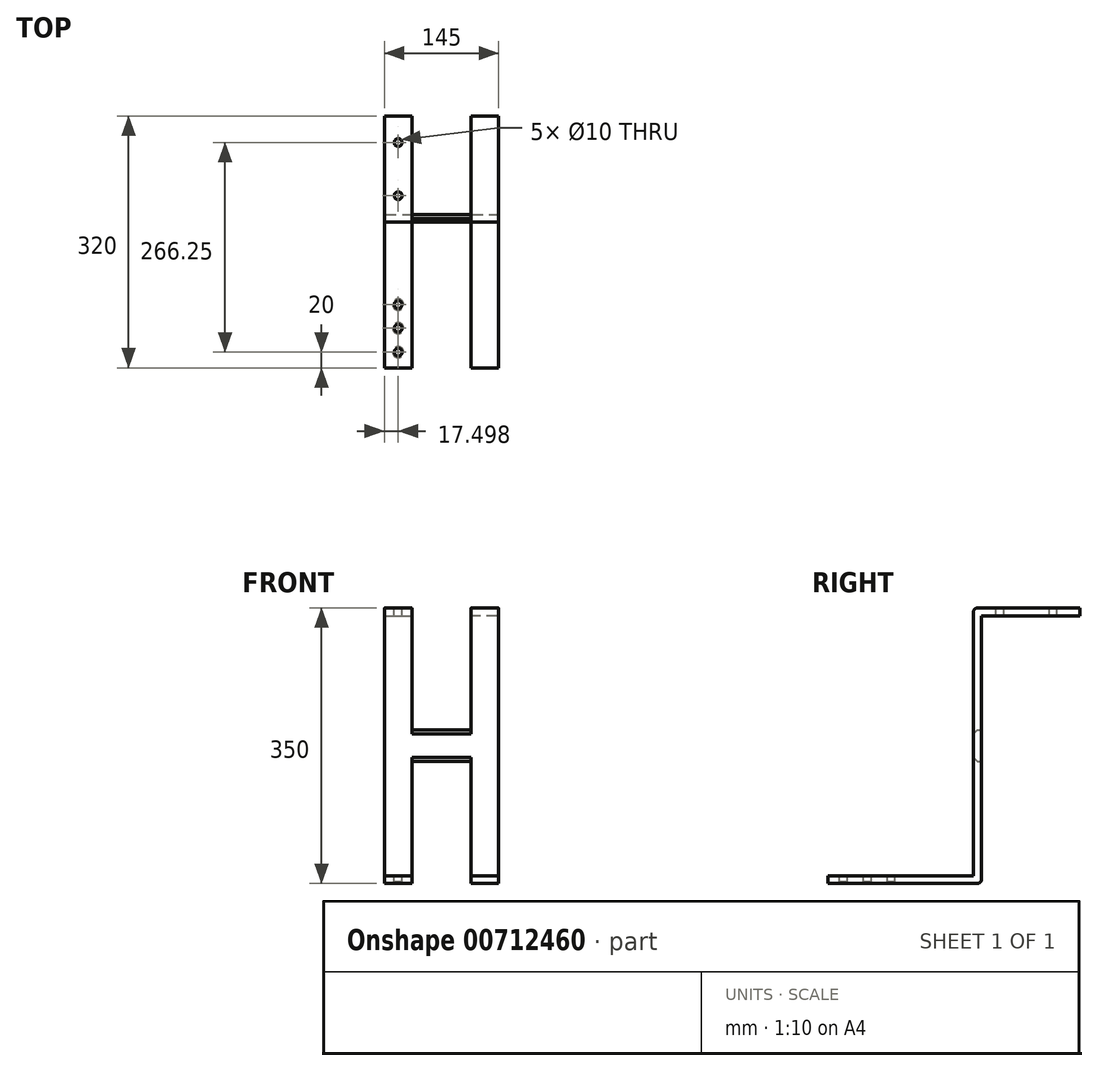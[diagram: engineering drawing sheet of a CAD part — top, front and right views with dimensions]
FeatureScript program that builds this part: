
annotation { "Feature Type Name" : "Feature", "Feature Type Description" : "" }
export const myFeature = defineFeature(function(context is Context, id is Id, definition is map)
    precondition{}
    {
        {
            var Q0;
            Q0=qCreatedBy(makeId("Front.planeOp"),FACE);
            var sketch = newSketch(context, id + "F0", { "sketchPlane" : qUnion([Q0])});
            skLineSegment(sketch, "E0.bottom", {"start": v(-69.95, 272.66) * mm, "end": v(-34.95, 272.66) * mm});
            skLineSegment(sketch, "E0.top", {"start": v(-69.95, -77.34) * mm, "end": v(-34.95, -77.34) * mm});
            skLineSegment(sketch, "E0.left", {"start": v(-69.95, 272.66) * mm, "end": v(-69.95, -77.34) * mm});
            skLineSegment(sketch, "E0.right", {"start": v(-34.95, 272.66) * mm, "end": v(-34.95, -77.34) * mm});
            skLineSegment(sketch, "E1.bottom", {"start": v(40.05, 272.66) * mm, "end": v(75.05, 272.66) * mm});
            skLineSegment(sketch, "E1.top", {"start": v(40.05, -77.34) * mm, "end": v(75.05, -77.34) * mm});
            skLineSegment(sketch, "E1.left", {"start": v(40.05, 272.66) * mm, "end": v(40.05, -77.34) * mm});
            skLineSegment(sketch, "E1.right", {"start": v(75.05, 272.66) * mm, "end": v(75.05, -77.34) * mm});
            skLineSegment(sketch, "E2", {"start": v(-34.95, 97.66) * mm, "end": v(-34.95, 117.66) * mm});
            skLineSegment(sketch, "E3.bottom", {"start": v(-34.95, 117.66) * mm, "end": v(40.05, 117.66) * mm});
            skLineSegment(sketch, "E3.top", {"start": v(-34.95, 77.66) * mm, "end": v(40.05, 77.66) * mm});
            skSolve(sketch);
        }
        {
            var Q0;
            Q0 = qSketchRegion(id + "F0", true);
            extrude(context, id + "F1", {"entities" : qUnion([Q0]), "depth" : 10 * mm, "offsetDistance" : 25 * mm});
        }
        {
            var Q0;
            Q0=makeQuery(id+"F1.opExtrude","CAP_FACE",FACE,{"disambiguationData":[OSD([sQuery(id+"F0.wireOp",EDGE,"E0.bottom"),sQuery(id+"F0.wireOp",EDGE,"E0.top"),sQuery(id+"F0.wireOp",EDGE,"E0.left"),sQuery(id+"F0.wireOp",EDGE,"E0.right"),sQuery(id+"F0.wireOp",EDGE,"E1.bottom"),sQuery(id+"F0.wireOp",EDGE,"E1.top"),sQuery(id+"F0.wireOp",EDGE,"E1.left"),sQuery(id+"F0.wireOp",EDGE,"E1.right"),sQuery(id+"F0.wireOp",EDGE,"E3.bottom"),sQuery(id+"F0.wireOp",EDGE,"E3.top")])],"isStart":false});
            var sketch = newSketch(context, id + "F2", { "sketchPlane" : qUnion([Q0])});
            skLineSegment(sketch, "E4", {"start": v(-69.95, -77.34) * mm, "end": v(-34.95, -77.34) * mm});
            skLineSegment(sketch, "E5", {"start": v(-34.95, -77.34) * mm, "end": v(-34.95, -67.34) * mm});
            skLineSegment(sketch, "E6.bottom", {"start": v(-34.95, -67.34) * mm, "end": v(-69.95, -67.34) * mm});
            skLineSegment(sketch, "E6.top", {"start": v(-34.95, -77.34) * mm, "end": v(-69.95, -77.34) * mm});
            skLineSegment(sketch, "E6.right", {"start": v(-69.95, -67.34) * mm, "end": v(-69.95, -77.34) * mm});
            skLineSegment(sketch, "E7", {"start": v(2.55, 77.66) * mm, "end": v(2.55, -129.94) * mm});
            skLineSegment(sketch, "E8.MirrorCS", {"start": v(40.05, -77.34) * mm, "end": v(40.05, -67.34) * mm});
            skLineSegment(sketch, "E9.MirrorCS", {"start": v(40.05, -77.34) * mm, "end": v(75.05, -77.34) * mm});
            skLineSegment(sketch, "E10.MirrorCS", {"start": v(40.05, -67.34) * mm, "end": v(75.05, -67.34) * mm});
            skLineSegment(sketch, "E11.MirrorCS", {"start": v(75.05, -67.34) * mm, "end": v(75.05, -77.34) * mm});
            skSolve(sketch);
        }
        {
            var Q0;
            Q0=makeQuery(id+"F2.imprint","IMPRINT",FACE,{"disambiguationData":[TD([[makeQuery(id+"F2.imprint","IMPRINT",EDGE,{"derivedFrom":sQuery(id+"F2.wireOp",EDGE,"E5")}),-1.0]])]});
            var Q1;
            Q1=makeQuery(id+"F2.imprint","IMPRINT",FACE,{"disambiguationData":[TD([[makeQuery(id+"F2.imprint","IMPRINT",EDGE,{"derivedFrom":sQuery(id+"F2.wireOp",EDGE,"E8.MirrorCS")}),1.0]])]});
            extrude(context, id + "F3", {"entities" : qUnion([Q0, Q1]), "operationType" : NewBodyOperationType.ADD, "depth" : 185 * mm, "offsetDistance" : 25 * mm});
        }
        {
            var Q0;
            Q0=makeQuery(id+"F3.opExtrude","SWEPT_FACE",FACE,{"disambiguationData":[OSD([sQuery(id+"F2.wireOp",EDGE,"E6.bottom")])]});
            var sketch = newSketch(context, id + "F4", { "sketchPlane" : qUnion([Q0])});
            skLineSegment(sketch, "E12", {"start": v(-34.95, -10) * mm, "end": v(40.05, -10) * mm});
            skLineSegment(sketch, "E13", {"start": v(2.55, -10) * mm, "end": v(2.55, -269.88) * mm});
            skLineSegment(sketch, "E14", {"start": v(-69.95, -195) * mm, "end": v(-69.95, -175) * mm});
            skLineSegment(sketch, "E15", {"start": v(-69.95, -175) * mm, "end": v(-69.95, -159.54) * mm});
            skLineSegment(sketch, "E16", {"start": v(-69.95, -159.54) * mm, "end": v(-69.95, -144.54) * mm});
            skLineSegment(sketch, "E17", {"start": v(-69.95, -144.54) * mm, "end": v(-69.95, -129.54) * mm});
            skLineSegment(sketch, "E18", {"start": v(-69.95, -129.54) * mm, "end": v(-69.95, -114.54) * mm});
            skLineSegment(sketch, "E19", {"start": v(-69.95, -114.54) * mm, "end": v(-69.95, -99.54) * mm});
            skCircle(sketch, "E20", {"center": v(-52.45, -114.54) * mm, "radius": 5 * mm});
            skCircle(sketch, "E21", {"center": v(-52.45, -144.54) * mm, "radius": 5 * mm});
            skCircle(sketch, "E22", {"center": v(-52.45, -175) * mm, "radius": 5 * mm});
            skCircle(sketch, "E23.MirrorC", {"center": v(57.55, -144.54) * mm, "radius": 5 * mm});
            skCircle(sketch, "E24.MirrorC", {"center": v(57.55, -175) * mm, "radius": 5 * mm});
            skCircle(sketch, "E25.MirrorC", {"center": v(57.55, -114.54) * mm, "radius": 5 * mm});
            skSolve(sketch);
        }
        {
            var Q0;
            Q0=makeQuery(id+"F4.imprint","IMPRINT",FACE,{"disambiguationData":[TD([[makeQuery(id+"F4.imprint","IMPRINT",EDGE,{"derivedFrom":sQuery(id+"F4.wireOp",EDGE,"E25.MirrorC")}),-1.0]])]});
            var Q1;
            Q1=makeQuery(id+"F4.imprint","IMPRINT",FACE,{"disambiguationData":[TD([[makeQuery(id+"F4.imprint","IMPRINT",EDGE,{"derivedFrom":sQuery(id+"F4.wireOp",EDGE,"E23.MirrorC")}),-1.0]])]});
            var Q2;
            Q2=makeQuery(id+"F4.imprint","IMPRINT",FACE,{"disambiguationData":[TD([[makeQuery(id+"F4.imprint","IMPRINT",EDGE,{"derivedFrom":sQuery(id+"F4.wireOp",EDGE,"E24.MirrorC")}),-1.0]])]});
            var Q3;
            Q3=makeQuery(id+"F4.imprint","IMPRINT",FACE,{"disambiguationData":[TD([[makeQuery(id+"F4.imprint","IMPRINT",EDGE,{"derivedFrom":sQuery(id+"F4.wireOp",EDGE,"E20")}),1.0]])]});
            var Q4;
            Q4=makeQuery(id+"F4.imprint","IMPRINT",FACE,{"disambiguationData":[TD([[makeQuery(id+"F4.imprint","IMPRINT",EDGE,{"derivedFrom":sQuery(id+"F4.wireOp",EDGE,"E21")}),1.0]])]});
            var Q5;
            Q5=makeQuery(id+"F4.imprint","IMPRINT",FACE,{"disambiguationData":[TD([[makeQuery(id+"F4.imprint","IMPRINT",EDGE,{"derivedFrom":sQuery(id+"F4.wireOp",EDGE,"E22")}),1.0]])]});
            extrude(context, id + "F5", {"entities" : qUnion([Q0, Q1, Q2, Q3, Q4, Q5]), "operationType" : NewBodyOperationType.REMOVE, "oppositeDirection" : true, "depth" : 25 * mm, "offsetDistance" : 25 * mm});
        }
        {
            var Q0;
            Q0=makeQuery(id+"F1.opExtrude","CAP_FACE",FACE,{"disambiguationData":[OSD([sQuery(id+"F0.wireOp",EDGE,"E0.bottom"),sQuery(id+"F0.wireOp",EDGE,"E0.top"),sQuery(id+"F0.wireOp",EDGE,"E0.left"),sQuery(id+"F0.wireOp",EDGE,"E0.right"),sQuery(id+"F0.wireOp",EDGE,"E1.bottom"),sQuery(id+"F0.wireOp",EDGE,"E1.top"),sQuery(id+"F0.wireOp",EDGE,"E1.left"),sQuery(id+"F0.wireOp",EDGE,"E1.right"),sQuery(id+"F0.wireOp",EDGE,"E3.bottom"),sQuery(id+"F0.wireOp",EDGE,"E3.top")])],"isStart":true});
            var sketch = newSketch(context, id + "F6", { "sketchPlane" : qUnion([Q0])});
            skLineSegment(sketch, "E26.bottom", {"start": v(-75.05, 272.66) * mm, "end": v(-40.05, 272.66) * mm});
            skLineSegment(sketch, "E26.top", {"start": v(-75.05, 262.66) * mm, "end": v(-40.05, 262.66) * mm});
            skLineSegment(sketch, "E26.left", {"start": v(-75.05, 272.66) * mm, "end": v(-75.05, 262.66) * mm});
            skLineSegment(sketch, "E26.right", {"start": v(-40.05, 272.66) * mm, "end": v(-40.05, 262.66) * mm});
            skLineSegment(sketch, "E27", {"start": v(-2.55, 195.16) * mm, "end": v(-2.55, 321.3) * mm});
            skLineSegment(sketch, "E28.MirrorCS", {"start": v(69.95, 262.66) * mm, "end": v(34.95, 262.66) * mm});
            skLineSegment(sketch, "E29.MirrorCS", {"start": v(34.95, 272.66) * mm, "end": v(34.95, 262.66) * mm});
            skLineSegment(sketch, "E30.MirrorCS", {"start": v(69.95, 272.66) * mm, "end": v(34.95, 272.66) * mm});
            skSolve(sketch);
        }
        {
            var Q0;
            Q0=makeQuery(id+"F6.imprint","IMPRINT",FACE,{"disambiguationData":[TD([[makeQuery(id+"F6.imprint","IMPRINT",EDGE,{"derivedFrom":sQuery(id+"F6.wireOp",EDGE,"E26.bottom")}),1.0]])]});
            var Q1;
            {var subQ0=sQuery(id+"F6.wireOp",EDGE,"E28.MirrorCS");Q1=makeQuery(id+"F6.imprint","IMPRINT",FACE,{"disambiguationData":[TD([[makeQuery(id+"F6.imprint","IMPRINT",EDGE,{"derivedFrom":subQ0}),-1.0]])]});}
            extrude(context, id + "F7", {"entities" : qUnion([Q0, Q1]), "operationType" : NewBodyOperationType.ADD, "depth" : 125 * mm, "offsetDistance" : 25 * mm});
        }
        {
            var Q0;
            Q0=makeQuery(id+"F7.boolean.opBoolean","MERGE",FACE,{"derivedFrom":[makeQuery(id+"F1.opExtrude","SWEPT_FACE",FACE,{"disambiguationData":[OSD([sQuery(id+"F0.wireOp",EDGE,"E0.bottom")])]}),makeQuery(id+"F7.opExtrude","SWEPT_FACE",FACE,{"disambiguationData":[OSD([sQuery(id+"F6.wireOp",EDGE,"E30.MirrorCS")])]})]});
            var sketch = newSketch(context, id + "F8", { "sketchPlane" : qUnion([Q0])});
            skLineSegment(sketch, "E31", {"start": v(-34.95, 57.5) * mm, "end": v(40.05, 57.5) * mm});
            skLineSegment(sketch, "E32", {"start": v(2.55, 57.5) * mm, "end": v(2.55, 287.25) * mm});
            skLineSegment(sketch, "E33", {"start": v(-34.95, 57.5) * mm, "end": v(-34.95, -10) * mm});
            skCircle(sketch, "E34", {"center": v(-52.45, 91.25) * mm, "radius": 5 * mm});
            skCircle(sketch, "E35", {"center": v(-52.45, 23.75) * mm, "radius": 5 * mm});
            skLineSegment(sketch, "E36", {"start": v(2.55, 57.5) * mm, "end": v(2.55, -29.78) * mm});
            skCircle(sketch, "E37.MirrorC", {"center": v(57.55, 23.75) * mm, "radius": 5 * mm});
            skCircle(sketch, "E38.MirrorC", {"center": v(57.55, 91.25) * mm, "radius": 5 * mm});
            skSolve(sketch);
        }
        {
            var Q0;
            Q0=makeQuery(id+"F8.imprint","IMPRINT",FACE,{"disambiguationData":[TD([[makeQuery(id+"F8.imprint","IMPRINT",EDGE,{"derivedFrom":sQuery(id+"F8.wireOp",EDGE,"E35")}),1.0]])]});
            var Q1;
            Q1=makeQuery(id+"F8.imprint","IMPRINT",FACE,{"disambiguationData":[TD([[makeQuery(id+"F8.imprint","IMPRINT",EDGE,{"derivedFrom":sQuery(id+"F8.wireOp",EDGE,"E34")}),1.0]])]});
            var Q2;
            Q2=makeQuery(id+"F8.imprint","IMPRINT",FACE,{"disambiguationData":[TD([[makeQuery(id+"F8.imprint","IMPRINT",EDGE,{"derivedFrom":sQuery(id+"F8.wireOp",EDGE,"E38.MirrorC")}),-1.0]])]});
            var Q3;
            Q3=makeQuery(id+"F8.imprint","IMPRINT",FACE,{"disambiguationData":[TD([[makeQuery(id+"F8.imprint","IMPRINT",EDGE,{"derivedFrom":sQuery(id+"F8.wireOp",EDGE,"E37.MirrorC")}),-1.0]])]});
            extrude(context, id + "F9", {"entities" : qUnion([Q0, Q1, Q2, Q3]), "operationType" : NewBodyOperationType.REMOVE, "oppositeDirection" : true, "depth" : 25 * mm, "offsetDistance" : 25 * mm});
        }
        {
            var Q0;
            Q0=makeQuery(id+"F1.opExtrude","CAP_EDGE",EDGE,{"disambiguationData":[OSD([sQuery(id+"F0.wireOp",EDGE,"E0.bottom")])],"isStart":false});
            var Q1;
            Q1=makeQuery(id+"F1.opExtrude","CAP_EDGE",EDGE,{"disambiguationData":[OSD([sQuery(id+"F0.wireOp",EDGE,"E1.bottom")])],"isStart":false});
            var Q2;
            Q2=makeQuery(id+"F3.opExtrude","CAP_EDGE",EDGE,{"disambiguationData":[OSD([sQuery(id+"F2.wireOp",EDGE,"E6.bottom")])],"isStart":true});
            var Q3;
            Q3=makeQuery(id+"F3.opExtrude","CAP_EDGE",EDGE,{"disambiguationData":[OSD([sQuery(id+"F2.wireOp",EDGE,"E10.MirrorCS")])],"isStart":true});
            var Q4;
            Q4=makeQuery(id+"F1.opExtrude","CAP_EDGE",EDGE,{"disambiguationData":[OSD([sQuery(id+"F0.wireOp",EDGE,"E0.top")])],"isStart":true});
            var Q5;
            Q5=makeQuery(id+"F1.opExtrude","CAP_EDGE",EDGE,{"disambiguationData":[OSD([sQuery(id+"F0.wireOp",EDGE,"E1.top")])],"isStart":true});
            var Q6;
            Q6=makeQuery(id+"F7.opExtrude","CAP_EDGE",EDGE,{"disambiguationData":[OSD([sQuery(id+"F6.wireOp",EDGE,"E28.MirrorCS")])],"isStart":true});
            var Q7;
            Q7=makeQuery(id+"F7.opExtrude","CAP_EDGE",EDGE,{"disambiguationData":[OSD([sQuery(id+"F6.wireOp",EDGE,"E26.top")])],"isStart":true});
            fillet(context, id + "F10", {"entities" : qUnion([Q0, Q1, Q2, Q3, Q4, Q5, Q6, Q7]), "radius" : 5 * mm, "tangentPropagation" : true, "allowEdgeOverflow" : false});
        }
        {
            var Q0;
            Q0=makeQuery(id+"F1.opExtrude","CAP_EDGE",EDGE,{"disambiguationData":[OSD([sQuery(id+"F0.wireOp",EDGE,"E3.top")])],"isStart":false});
            var Q1;
            Q1=makeQuery(id+"F1.opExtrude","CAP_EDGE",EDGE,{"disambiguationData":[OSD([sQuery(id+"F0.wireOp",EDGE,"E3.bottom")])],"isStart":false});
            chamfer(context, id + "F11", {"entities" : qUnion([Q0, Q1]), "width" : 5 * mm, "tangentPropagation" : true});
        }
        {
            var Q0;
            Q0=makeQuery(id+"F9.boolean.opBoolean","COPY",EDGE,{"derivedFrom":makeQuery(id+"F9.opExtrude","CAP_EDGE",EDGE,{"disambiguationData":[OSD([sQuery(id+"F8.wireOp",EDGE,"E37.MirrorC")])],"isStart":true})});
            var Q1;
            Q1=makeQuery(id+"F9.boolean.opBoolean","COPY",EDGE,{"derivedFrom":makeQuery(id+"F9.opExtrude","CAP_EDGE",EDGE,{"disambiguationData":[OSD([sQuery(id+"F8.wireOp",EDGE,"E38.MirrorC")])],"isStart":true})});
            var Q2;
            Q2=makeQuery(id+"F9.boolean.opBoolean","COPY",EDGE,{"derivedFrom":makeQuery(id+"F9.opExtrude","CAP_EDGE",EDGE,{"disambiguationData":[OSD([sQuery(id+"F8.wireOp",EDGE,"E35")])],"isStart":true})});
            var Q3;
            Q3=makeQuery(id+"F9.boolean.opBoolean","COPY",EDGE,{"derivedFrom":makeQuery(id+"F9.opExtrude","CAP_EDGE",EDGE,{"disambiguationData":[OSD([sQuery(id+"F8.wireOp",EDGE,"E34")])],"isStart":true})});
            var Q4;
            Q4=makeQuery(id+"F5.boolean.opBoolean","INTERSECT",EDGE,{"derivedFrom":[makeQuery(id+"F3.boolean.opBoolean","MERGE",FACE,{"derivedFrom":[makeQuery(id+"F1.opExtrude","SWEPT_FACE",FACE,{"disambiguationData":[OSD([sQuery(id+"F0.wireOp",EDGE,"E0.top")])]}),makeQuery(id+"F3.opExtrude","SWEPT_FACE",FACE,{"disambiguationData":[OSD([sQuery(id+"F2.wireOp",EDGE,"E6.top")])]})]}),makeQuery(id+"F5.opExtrude","SWEPT_FACE",FACE,{"disambiguationData":[OSD([sQuery(id+"F4.wireOp",EDGE,"E22")])]})]});
            var Q5;
            Q5=makeQuery(id+"F5.boolean.opBoolean","INTERSECT",EDGE,{"derivedFrom":[makeQuery(id+"F3.boolean.opBoolean","MERGE",FACE,{"derivedFrom":[makeQuery(id+"F1.opExtrude","SWEPT_FACE",FACE,{"disambiguationData":[OSD([sQuery(id+"F0.wireOp",EDGE,"E0.top")])]}),makeQuery(id+"F3.opExtrude","SWEPT_FACE",FACE,{"disambiguationData":[OSD([sQuery(id+"F2.wireOp",EDGE,"E6.top")])]})]}),makeQuery(id+"F5.opExtrude","SWEPT_FACE",FACE,{"disambiguationData":[OSD([sQuery(id+"F4.wireOp",EDGE,"E21")])]})]});
            var Q6;
            Q6=makeQuery(id+"F5.boolean.opBoolean","INTERSECT",EDGE,{"derivedFrom":[makeQuery(id+"F3.boolean.opBoolean","MERGE",FACE,{"derivedFrom":[makeQuery(id+"F1.opExtrude","SWEPT_FACE",FACE,{"disambiguationData":[OSD([sQuery(id+"F0.wireOp",EDGE,"E0.top")])]}),makeQuery(id+"F3.opExtrude","SWEPT_FACE",FACE,{"disambiguationData":[OSD([sQuery(id+"F2.wireOp",EDGE,"E6.top")])]})]}),makeQuery(id+"F5.opExtrude","SWEPT_FACE",FACE,{"disambiguationData":[OSD([sQuery(id+"F4.wireOp",EDGE,"E20")])]})]});
            var Q7;
            Q7=makeQuery(id+"F5.boolean.opBoolean","INTERSECT",EDGE,{"derivedFrom":[makeQuery(id+"F3.boolean.opBoolean","MERGE",FACE,{"derivedFrom":[makeQuery(id+"F1.opExtrude","SWEPT_FACE",FACE,{"disambiguationData":[OSD([sQuery(id+"F0.wireOp",EDGE,"E1.top")])]}),makeQuery(id+"F3.opExtrude","SWEPT_FACE",FACE,{"disambiguationData":[OSD([sQuery(id+"F2.wireOp",EDGE,"E9.MirrorCS")])]})]}),makeQuery(id+"F5.opExtrude","SWEPT_FACE",FACE,{"disambiguationData":[OSD([sQuery(id+"F4.wireOp",EDGE,"E25.MirrorC")])]})]});
            var Q8;
            Q8=makeQuery(id+"F5.boolean.opBoolean","INTERSECT",EDGE,{"derivedFrom":[makeQuery(id+"F3.boolean.opBoolean","MERGE",FACE,{"derivedFrom":[makeQuery(id+"F1.opExtrude","SWEPT_FACE",FACE,{"disambiguationData":[OSD([sQuery(id+"F0.wireOp",EDGE,"E1.top")])]}),makeQuery(id+"F3.opExtrude","SWEPT_FACE",FACE,{"disambiguationData":[OSD([sQuery(id+"F2.wireOp",EDGE,"E9.MirrorCS")])]})]}),makeQuery(id+"F5.opExtrude","SWEPT_FACE",FACE,{"disambiguationData":[OSD([sQuery(id+"F4.wireOp",EDGE,"E23.MirrorC")])]})]});
            var Q9;
            Q9=makeQuery(id+"F5.boolean.opBoolean","INTERSECT",EDGE,{"derivedFrom":[makeQuery(id+"F3.boolean.opBoolean","MERGE",FACE,{"derivedFrom":[makeQuery(id+"F1.opExtrude","SWEPT_FACE",FACE,{"disambiguationData":[OSD([sQuery(id+"F0.wireOp",EDGE,"E1.top")])]}),makeQuery(id+"F3.opExtrude","SWEPT_FACE",FACE,{"disambiguationData":[OSD([sQuery(id+"F2.wireOp",EDGE,"E9.MirrorCS")])]})]}),makeQuery(id+"F5.opExtrude","SWEPT_FACE",FACE,{"disambiguationData":[OSD([sQuery(id+"F4.wireOp",EDGE,"E24.MirrorC")])]})]});
            chamfer(context, id + "F12", {"entities" : qUnion([Q0, Q1, Q2, Q3, Q4, Q5, Q6, Q7, Q8, Q9]), "width" : 2 * mm, "tangentPropagation" : true});
        }
    });
